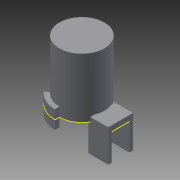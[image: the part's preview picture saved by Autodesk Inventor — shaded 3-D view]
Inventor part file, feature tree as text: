
AUTODESK INVENTOR PART (.ipt)
format: ipt  version: 2013 (Build 170138000, 138)  size: 163,840 bytes
history: native  units: mm
features: sketch x7, extrude x6, other x1
ambient origin geometry x8: Origin, YZ Plane, XZ Plane, XY Plane, X Axis, Y Axis, Z Axis, Center Point
feature tree (14):
  other  "ソリッド1"
  extrude  "押し出し1"  Depth=9.768mm
  extrude  "押し出し2"  Depth=15.0mm
  extrude  "押し出し3"  Depth=2.0mm
  extrude  "押し出し4"  Depth=18.0mm
  sketch  "スケッチ5"
  extrude  "押し出し5"  Depth=13.768mm
  extrude  "押し出し6"  Depth=10.0mm TaperAngle=0.0deg
  sketch  "スケッチ1"
  sketch  "スケッチ2"
  sketch  "スケッチ3"
  sketch  "スケッチ4"
  sketch  "スケッチ6"
  sketch  "スケッチ7"
